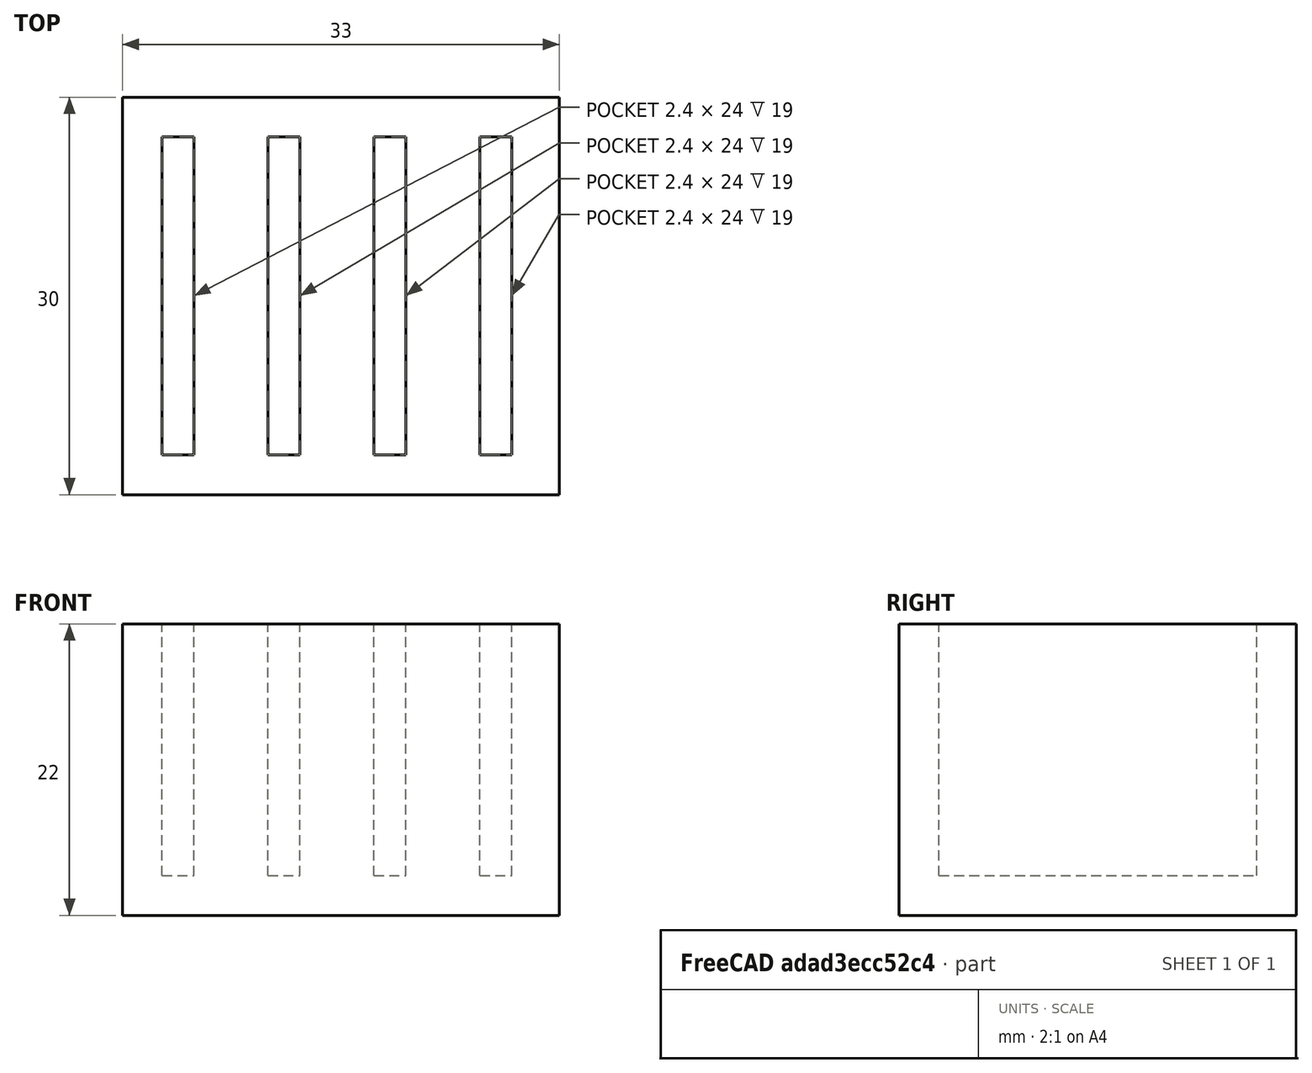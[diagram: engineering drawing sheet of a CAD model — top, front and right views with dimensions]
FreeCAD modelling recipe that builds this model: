
FCSTD DOCUMENT  (FreeCAD 1.0R39319 (Git))
Label: ojt1_t08r01_sd_holder
License: All rights reserved
LicenseURL: https://en.wikipedia.org/wiki/All_rights_reserved
objects: Part::Box×5, Part::MultiFuse×1, Part::Cut×1
note: 7 computed .brp shape members not serialized (recipe doc carries the construction recipe); baked Part::Feature solids carry a one-line shape summary decoded from their .brp

FEATURE [Part::Box] Box  label="Cubo"
  AttacherType = Attacher::AttachEngine3D
  Height = 22
  Length = 33
  Width = 30
FEATURE [Part::Box] Box001  label="Cubo001"
  AttacherType = Attacher::AttachEngine3D
  Height = 19
  Length = 2.4
  Placement = pos=(3,3,3) rot=(0,0,1;0rad)
  Width = 24
FEATURE [Part::Box] Box002  label="Cubo002"
  AttacherType = Attacher::AttachEngine3D
  Height = 19
  Length = 2.4
  Placement = pos=(11,3,3) rot=(0,0,1;0rad)
  Width = 24
FEATURE [Part::Box] Box003  label="Cubo003"
  AttacherType = Attacher::AttachEngine3D
  Height = 19
  Length = 2.4
  Placement = pos=(19,3,3) rot=(0,0,1;0rad)
  Width = 24
FEATURE [Part::Box] Box004  label="Cubo004"
  AttacherType = Attacher::AttachEngine3D
  Height = 19
  Length = 2.4
  Placement = pos=(27,3,3) rot=(0,0,1;0rad)
  Width = 24
FEATURE [Part::MultiFuse] Fusion
  Refine = true
  Shapes = -> [Box004,Box003,Box002,Box001]
FEATURE [Part::Cut] Cut
  Base = -> Box
  Refine = true
  Tool = -> Fusion
